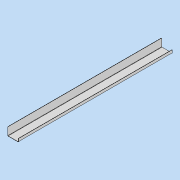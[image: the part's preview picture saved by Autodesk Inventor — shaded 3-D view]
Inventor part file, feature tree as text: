
AUTODESK INVENTOR PART (.ipt)
format: ipt  version: 2020 (Build 240168000, 168)  size: 118,784 bytes
history: native  units: mm
features: other x10, sketch x3, fillet x1
ambient origin geometry x8: Origin, YZ Plane, XZ Plane, XY Plane, X Axis, Y Axis, Z Axis, Center Point
bodies: Body1 (feature_tree)
feature tree (14):
  other  "ソリッド1"
  other  "フランジ1"
  other  "フランジ2"
  fillet  "フィレット1"  Radius=52.0mm
  sketch  "スケッチ1"
  other  "プレート1"
  sketch  "スケッチ2"
  other  "プレート2"
  other  "曲げ1"
  other  "コーナー1"
  sketch  "スケッチ3"
  other  "プレート3"
  other  "曲げ2"
  other  "コーナー2"
